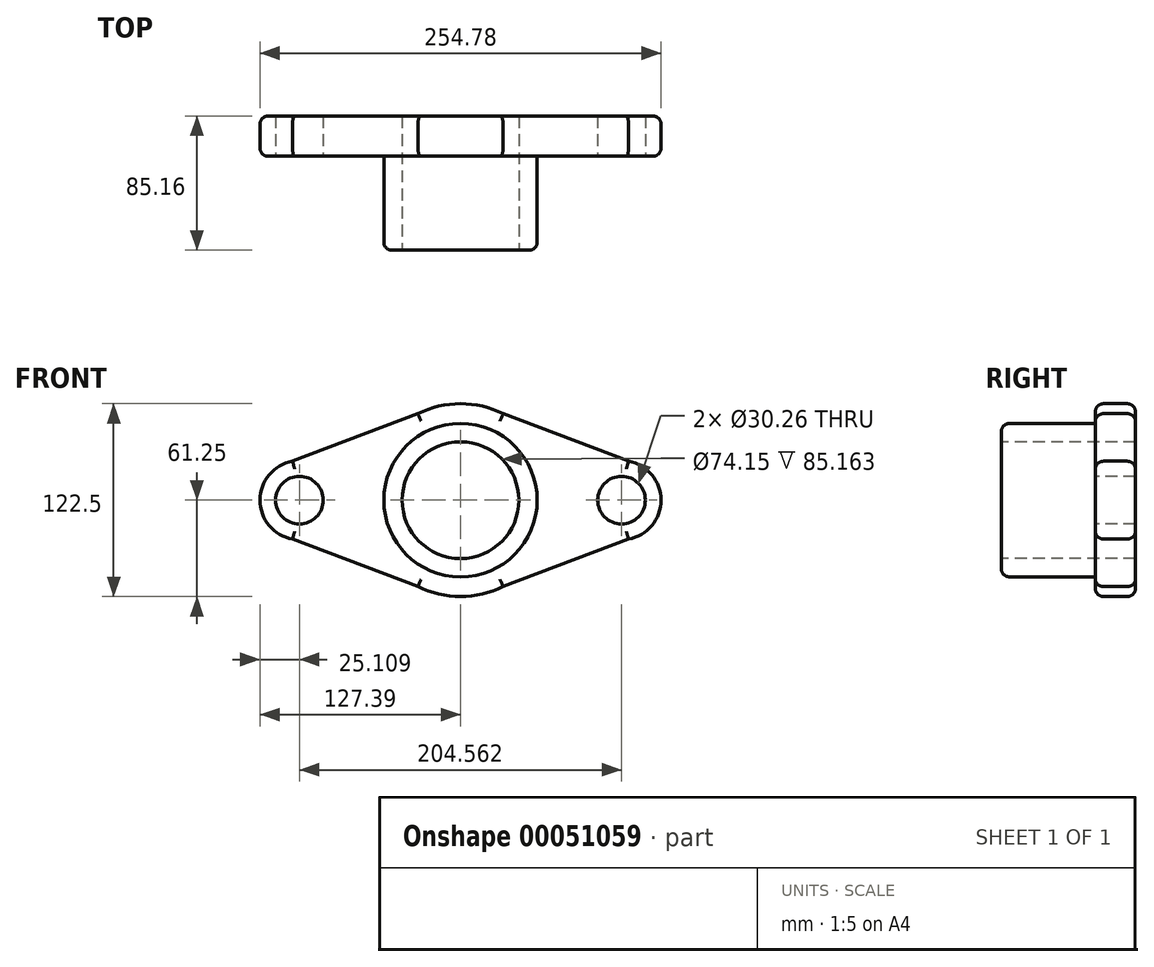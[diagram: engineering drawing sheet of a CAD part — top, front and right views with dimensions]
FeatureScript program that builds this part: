
annotation { "Feature Type Name" : "Feature", "Feature Type Description" : "" }
export const myFeature = defineFeature(function(context is Context, id is Id, definition is map)
    precondition{}
    {
        {
            var Q0;
            Q0=qCreatedBy(makeId("Front.planeOp"),FACE);
            var sketch = newSketch(context, id + "F0", { "sketchPlane" : qUnion([Q0])});
            skArc(sketch, "E0", {"start": v(-27.12, -54.92) * mm, "mid": v(0, -61.25) * mm, "end": v(27.12, -54.92) * mm});
            skArc(sketch, "E1", {"start": v(-106.7, 24.72) * mm, "mid": v(-127.4, 0) * mm, "end": v(-106.7, -24.72) * mm});
            skArc(sketch, "E2.MirrorC", {"start": v(106.7, 24.72) * mm, "mid": v(127.4, 0) * mm, "end": v(106.7, -24.72) * mm});
            skLineSegment(sketch, "E3", {"start": v(-106.7, 24.72) * mm, "end": v(-27.12, 54.92) * mm});
            skLineSegment(sketch, "E4.MirrorCS", {"start": v(-106.7, -24.72) * mm, "end": v(-27.12, -54.92) * mm});
            skLineSegment(sketch, "E5.MirrorCS", {"start": v(106.7, 24.72) * mm, "end": v(27.12, 54.92) * mm});
            skLineSegment(sketch, "E6.MirrorCS", {"start": v(106.7, -24.72) * mm, "end": v(27.12, -54.92) * mm});
            skArc(sketch, "E7.trimOffspring", {"start": v(27.12, 54.92) * mm, "mid": v(0, 61.25) * mm, "end": v(-27.12, 54.92) * mm});
            skSolve(sketch);
        }
        {
            var Q0;
            Q0 = qSketchRegion(id + "F0", true);
            extrude(context, id + "F1", {"entities" : qUnion([Q0]), "depth" : 25.4 * mm});
        }
        {
            var Q0;
            Q0=makeQuery(id+"F1.opExtrude","CAP_FACE",FACE,{"disambiguationData":[OSD([sQuery(id+"F0.wireOp",EDGE,"E0"),sQuery(id+"F0.wireOp",EDGE,"E1"),sQuery(id+"F0.wireOp",EDGE,"E2.MirrorC"),sQuery(id+"F0.wireOp",EDGE,"E3"),sQuery(id+"F0.wireOp",EDGE,"E4.MirrorCS"),sQuery(id+"F0.wireOp",EDGE,"E5.MirrorCS"),sQuery(id+"F0.wireOp",EDGE,"E6.MirrorCS"),sQuery(id+"F0.wireOp",EDGE,"E7.trimOffspring")])],"isStart":false});
            var sketch = newSketch(context, id + "F2", { "sketchPlane" : qUnion([Q0])});
            skCircle(sketch, "E8", {"center": v(0, 0) * mm, "radius": 48.7 * mm});
            skSolve(sketch);
        }
        {
            var Q0;
            Q0 = qSketchRegion(id + "F2", true);
            extrude(context, id + "F3", {"entities" : qUnion([Q0]), "operationType" : NewBodyOperationType.ADD, "depth" : 59.76 * mm});
        }
        {
            var Q0;
            Q0=makeQuery(id+"F1.opExtrude","CAP_FACE",FACE,{"disambiguationData":[OSD([sQuery(id+"F0.wireOp",EDGE,"E0"),sQuery(id+"F0.wireOp",EDGE,"E1"),sQuery(id+"F0.wireOp",EDGE,"E2.MirrorC"),sQuery(id+"F0.wireOp",EDGE,"E3"),sQuery(id+"F0.wireOp",EDGE,"E4.MirrorCS"),sQuery(id+"F0.wireOp",EDGE,"E5.MirrorCS"),sQuery(id+"F0.wireOp",EDGE,"E6.MirrorCS"),sQuery(id+"F0.wireOp",EDGE,"E7.trimOffspring")])],"isStart":false});
            var sketch = newSketch(context, id + "F4", { "sketchPlane" : qUnion([Q0])});
            skCircle(sketch, "E9", {"center": v(-102.28, 0) * mm, "radius": 15.13 * mm});
            skCircle(sketch, "E10.MirrorC", {"center": v(102.28, 0) * mm, "radius": 15.13 * mm});
            skSolve(sketch);
        }
        {
            var Q0;
            Q0 = qSketchRegion(id + "F4", true);
            extrude(context, id + "F5", {"entities" : qUnion([Q0]), "operationType" : NewBodyOperationType.REMOVE, "oppositeDirection" : true, "depth" : 25.4 * mm});
        }
        {
            var Q0;
            Q0=makeQuery(id+"F3.opExtrude","CAP_FACE",FACE,{"disambiguationData":[OSD([sQuery(id+"F2.wireOp",EDGE,"E8")])],"isStart":false});
            var sketch = newSketch(context, id + "F6", { "sketchPlane" : qUnion([Q0])});
            skCircle(sketch, "E11", {"center": v(0, 0) * mm, "radius": 37.08 * mm});
            skSolve(sketch);
        }
        {
            var Q0;
            Q0 = qSketchRegion(id + "F6", true);
            extrude(context, id + "F7", {"entities" : qUnion([Q0]), "operationType" : NewBodyOperationType.REMOVE, "oppositeDirection" : true, "depth" : 170.47 * mm});
        }
        {
            var Q0;
            Q0=makeQuery(id+"F3.opExtrude","CAP_EDGE",EDGE,{"disambiguationData":[OSD([sQuery(id+"F2.wireOp",EDGE,"E8")])],"isStart":true});
            var Q1;
            Q1=makeQuery(id+"F3.opExtrude","CAP_EDGE",EDGE,{"disambiguationData":[OSD([sQuery(id+"F2.wireOp",EDGE,"E8")])],"isStart":false});
            var Q2;
            Q2=makeQuery(id+"F7.boolean.opBoolean","COPY",EDGE,{"derivedFrom":makeQuery(id+"F7.opExtrude","CAP_EDGE",EDGE,{"disambiguationData":[OSD([sQuery(id+"F6.wireOp",EDGE,"E11")])],"isStart":true})});
            var Q3;
            Q3=makeQuery(id+"F5.boolean.opBoolean","COPY",EDGE,{"derivedFrom":makeQuery(id+"F5.opExtrude","CAP_EDGE",EDGE,{"disambiguationData":[OSD([sQuery(id+"F4.wireOp",EDGE,"E9")])],"isStart":true})});
            var Q4;
            Q4=makeQuery(id+"F5.boolean.opBoolean","COPY",EDGE,{"derivedFrom":makeQuery(id+"F5.opExtrude","CAP_EDGE",EDGE,{"disambiguationData":[OSD([sQuery(id+"F4.wireOp",EDGE,"E10.MirrorC")])],"isStart":true})});
            fillet(context, id + "F8", {"entities" : qUnion([Q0, Q1, Q2, Q3, Q4]), "radius" : 5.08 * mm, "tangentPropagation" : true, "allowEdgeOverflow" : false});
        }
        {
            var Q0;
            Q0=makeQuery(id+"F1.opExtrude","CAP_EDGE",EDGE,{"disambiguationData":[OSD([sQuery(id+"F0.wireOp",EDGE,"E3")])],"isStart":false});
            var Q1;
            Q1=makeQuery(id+"F1.opExtrude","CAP_EDGE",EDGE,{"disambiguationData":[OSD([sQuery(id+"F0.wireOp",EDGE,"E1")])],"isStart":false});
            var Q2;
            Q2=makeQuery(id+"F1.opExtrude","CAP_EDGE",EDGE,{"disambiguationData":[OSD([sQuery(id+"F0.wireOp",EDGE,"E4.MirrorCS")])],"isStart":false});
            var Q3;
            Q3=makeQuery(id+"F1.opExtrude","CAP_EDGE",EDGE,{"disambiguationData":[OSD([sQuery(id+"F0.wireOp",EDGE,"E7.trimOffspring")])],"isStart":false});
            var Q4;
            Q4=makeQuery(id+"F1.opExtrude","CAP_EDGE",EDGE,{"disambiguationData":[OSD([sQuery(id+"F0.wireOp",EDGE,"E5.MirrorCS")])],"isStart":false});
            var Q5;
            Q5=makeQuery(id+"F1.opExtrude","CAP_EDGE",EDGE,{"disambiguationData":[OSD([sQuery(id+"F0.wireOp",EDGE,"E2.MirrorC")])],"isStart":false});
            var Q6;
            Q6=makeQuery(id+"F1.opExtrude","CAP_EDGE",EDGE,{"disambiguationData":[OSD([sQuery(id+"F0.wireOp",EDGE,"E6.MirrorCS")])],"isStart":false});
            var Q7;
            Q7=makeQuery(id+"F1.opExtrude","CAP_EDGE",EDGE,{"disambiguationData":[OSD([sQuery(id+"F0.wireOp",EDGE,"E0")])],"isStart":false});
            var Q8;
            Q8=makeQuery(id+"F1.opExtrude","CAP_EDGE",EDGE,{"disambiguationData":[OSD([sQuery(id+"F0.wireOp",EDGE,"E2.MirrorC")])],"isStart":true});
            var Q9;
            Q9=makeQuery(id+"F1.opExtrude","CAP_EDGE",EDGE,{"disambiguationData":[OSD([sQuery(id+"F0.wireOp",EDGE,"E6.MirrorCS")])],"isStart":true});
            var Q10;
            Q10=makeQuery(id+"F1.opExtrude","CAP_EDGE",EDGE,{"disambiguationData":[OSD([sQuery(id+"F0.wireOp",EDGE,"E0")])],"isStart":true});
            var Q11;
            Q11=makeQuery(id+"F1.opExtrude","CAP_EDGE",EDGE,{"disambiguationData":[OSD([sQuery(id+"F0.wireOp",EDGE,"E4.MirrorCS")])],"isStart":true});
            var Q12;
            Q12=makeQuery(id+"F1.opExtrude","CAP_EDGE",EDGE,{"disambiguationData":[OSD([sQuery(id+"F0.wireOp",EDGE,"E1")])],"isStart":true});
            var Q13;
            Q13=makeQuery(id+"F1.opExtrude","CAP_EDGE",EDGE,{"disambiguationData":[OSD([sQuery(id+"F0.wireOp",EDGE,"E3")])],"isStart":true});
            var Q14;
            Q14=makeQuery(id+"F1.opExtrude","CAP_EDGE",EDGE,{"disambiguationData":[OSD([sQuery(id+"F0.wireOp",EDGE,"E7.trimOffspring")])],"isStart":true});
            var Q15;
            Q15=makeQuery(id+"F1.opExtrude","CAP_EDGE",EDGE,{"disambiguationData":[OSD([sQuery(id+"F0.wireOp",EDGE,"E5.MirrorCS")])],"isStart":true});
            fillet(context, id + "F9", {"entities" : qUnion([Q0, Q1, Q2, Q3, Q4, Q5, Q6, Q7, Q8, Q9, Q10, Q11, Q12, Q13, Q14, Q15]), "radius" : 5.08 * mm, "tangentPropagation" : true, "allowEdgeOverflow" : false});
        }
    });
